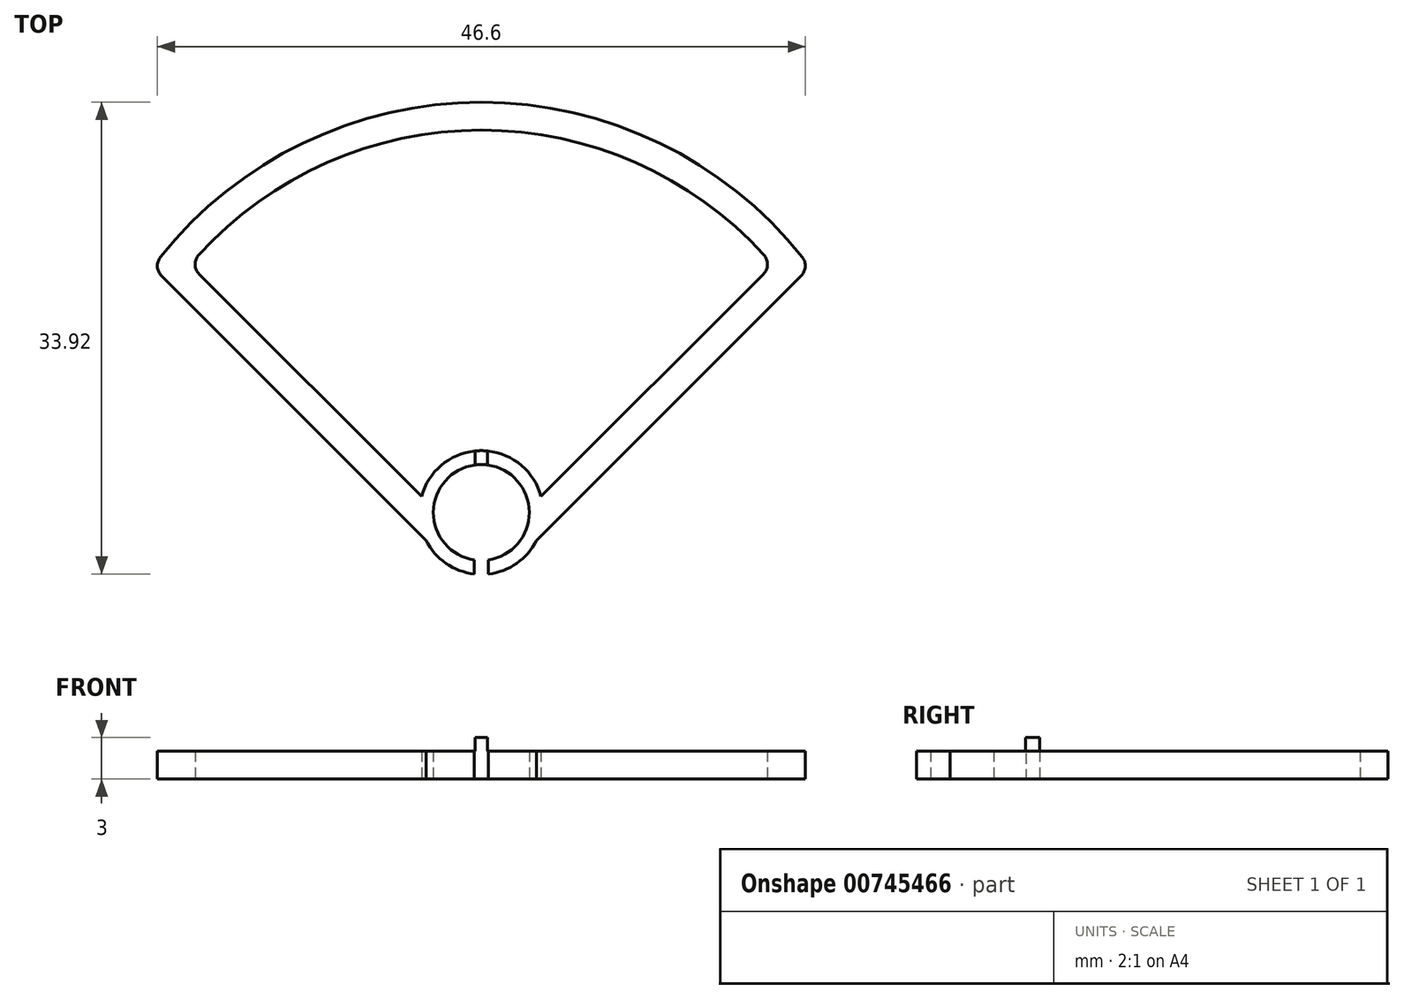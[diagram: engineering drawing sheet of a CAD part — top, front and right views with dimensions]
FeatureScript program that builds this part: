
annotation { "Feature Type Name" : "Feature", "Feature Type Description" : "" }
export const myFeature = defineFeature(function(context is Context, id is Id, definition is map)
    precondition{}
    {
        {
            var Q0;
            Q0=qCreatedBy(makeId("Top.planeOp"),FACE);
            var sketch = newSketch(context, id + "F0", { "sketchPlane" : qUnion([Q0])});
            skArc(sketch, "E0", {"start": v(0.5, -4.42) * mm, "mid": v(0, 4.45) * mm, "end": v(-0.5, -4.42) * mm});
            skLineSegment(sketch, "E1", {"start": v(-3.98, -2) * mm, "end": v(-23.63, 17.66) * mm});
            skLineSegment(sketch, "E2", {"start": v(3.98, -2) * mm, "end": v(23.63, 17.66) * mm});
            skArc(sketch, "E3", {"start": v(23.63, 17.66) * mm, "mid": v(0, 29.5) * mm, "end": v(-23.63, 17.66) * mm});
            skLineSegment(sketch, "E4.0", {"start": v(-4.3, 1.15) * mm, "end": v(-20.96, 17.8) * mm});
            skArc(sketch, "E4.1", {"start": v(20.96, 17.8) * mm, "mid": v(0, 27.5) * mm, "end": v(-20.96, 17.8) * mm});
            skLineSegment(sketch, "E4.2", {"start": v(4.3, 1.15) * mm, "end": v(20.96, 17.8) * mm});
            skArc(sketch, "E5", {"start": v(0.5, -3.41) * mm, "mid": v(0, 3.45) * mm, "end": v(-0.5, -3.41) * mm});
            skLineSegment(sketch, "E6", {"start": v(-0.5, -3.41) * mm, "end": v(-0.5, -4.42) * mm});
            skLineSegment(sketch, "E7", {"start": v(0.5, -3.41) * mm, "end": v(0.5, -4.42) * mm});
            skSolve(sketch);
        }
        {
            var Q0;
            {var subQ0=sQuery(id+"F0.wireOp",EDGE,"E1");Q0=makeQuery(id+"F0.imprint","IMPRINT",FACE,{"disambiguationData":[TD([[makeQuery(id+"F0.imprint","IMPRINT",EDGE,{"derivedFrom":subQ0}),-1.0]])]});}
            var Q1;
            Q1=makeQuery(id+"F0.imprint","IMPRINT",FACE,{"disambiguationData":[TD([[makeQuery(id+"F0.imprint","IMPRINT",EDGE,{"derivedFrom":sQuery(id+"F0.wireOp",EDGE,"E5")}),-1.0]])]});
            extrude(context, id + "F1", {"entities" : qUnion([Q0, Q1]), "depth" : 2 * mm, "offsetDistance" : 25 * mm});
        }
        {
            var Q0;
            Q0=makeQuery(id+"F1.opExtrude","CAP_FACE",FACE,{"disambiguationData":[OSD([sQuery(id+"F0.wireOp",EDGE,"E0"),sQuery(id+"F0.wireOp",EDGE,"E1"),sQuery(id+"F0.wireOp",EDGE,"E2"),sQuery(id+"F0.wireOp",EDGE,"E3"),sQuery(id+"F0.wireOp",EDGE,"E4.0"),sQuery(id+"F0.wireOp",EDGE,"E4.1"),sQuery(id+"F0.wireOp",EDGE,"E4.2"),sQuery(id+"F0.wireOp",EDGE,"E5"),sQuery(id+"F0.wireOp",EDGE,"E6"),sQuery(id+"F0.wireOp",EDGE,"E7")])],"isStart":false});
            var sketch = newSketch(context, id + "F2", { "sketchPlane" : qUnion([Q0])});
            skArc(sketch, "E8.0", {"start": v(0.45, 4.43) * mm, "mid": v(0, 4.45) * mm, "end": v(-0.45, 4.43) * mm});
            skArc(sketch, "E9.0", {"start": v(0.45, 3.42) * mm, "mid": v(0, 3.45) * mm, "end": v(-0.45, 3.42) * mm});
            skLineSegment(sketch, "E10", {"start": v(-0.45, 4.43) * mm, "end": v(-0.45, 3.42) * mm});
            skLineSegment(sketch, "E11", {"start": v(0.45, 4.43) * mm, "end": v(0.45, 3.42) * mm});
            skPoint(sketch, "E12.orphan", {"position": v(-4.3, 1.15) * mm});
            skPoint(sketch, "E13.orphan", {"position": v(4.3, 1.15) * mm});
            skPoint(sketch, "E14.orphan", {"position": v(0.5, -3.41) * mm});
            skPoint(sketch, "E15.orphan", {"position": v(-0.5, -3.41) * mm});
            skSolve(sketch);
        }
        {
            var Q0;
            Q0=makeQuery(id+"F2.imprint","IMPRINT",FACE,{"disambiguationData":[TD([[makeQuery(id+"F2.imprint","IMPRINT",EDGE,{"derivedFrom":sQuery(id+"F2.wireOp",EDGE,"E8.0")}),1.0]])]});
            extrude(context, id + "F3", {"entities" : qUnion([Q0]), "operationType" : NewBodyOperationType.ADD, "depth" : 1 * mm, "offsetDistance" : 25 * mm});
        }
        {
            var Q0;
            Q0=makeQuery(id+"F1.opExtrude","SWEPT_EDGE",EDGE,{"disambiguationData":[OSD([sQuery(id+"F0.wireOp",EDGE,"E1"),sQuery(id+"F0.wireOp",EDGE,"E3")])]});
            var Q1;
            Q1=makeQuery(id+"F1.opExtrude","SWEPT_EDGE",EDGE,{"disambiguationData":[OSD([sQuery(id+"F0.wireOp",EDGE,"E4.0"),sQuery(id+"F0.wireOp",EDGE,"E4.1")])]});
            var Q2;
            Q2=makeQuery(id+"F1.opExtrude","SWEPT_EDGE",EDGE,{"disambiguationData":[OSD([sQuery(id+"F0.wireOp",EDGE,"E2"),sQuery(id+"F0.wireOp",EDGE,"E3")])]});
            var Q3;
            Q3=makeQuery(id+"F1.opExtrude","SWEPT_EDGE",EDGE,{"disambiguationData":[OSD([sQuery(id+"F0.wireOp",EDGE,"E4.1"),sQuery(id+"F0.wireOp",EDGE,"E4.2")])]});
            fillet(context, id + "F4", {"entities" : qUnion([Q0, Q1, Q2, Q3]), "radius" : 1 * mm, "tangentPropagation" : true, "allowEdgeOverflow" : false});
        }
    });
